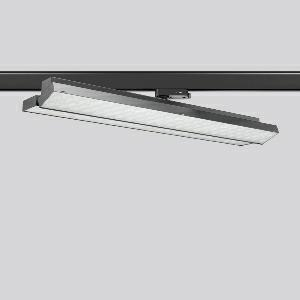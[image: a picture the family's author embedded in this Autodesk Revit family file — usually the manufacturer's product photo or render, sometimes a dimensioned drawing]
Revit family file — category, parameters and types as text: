
# Revit family: tx-move_742161_003_1_d967
name_source: partatom
category: Lighting Fixtures
units: mm (PartAtom-declared; Revit-internal decimal feet)

## family parameters
Cut with Voids When Loaded = No
Host = Face
Light Source = No
Part Type = Normal
Room Calculation Point = No
Round Connector Dimension = Use Diameter
Shared = No

## types (1)
- MultiLumen 1 (1 x LED Modul 840, 3125 lm, 4000)
    Apparent Load = 41 VA
    CIE Flux Codes = 90 97 99 100 100
    Color Rendering = 80
    Color Temperature = 4000
    Default Elevation = 1800 mm
    Description = Series: TX-MOVE
Multifunctional surface-mounted spotlight for area lighting. Very flat design. Housing: sheet steel, powder-coated. Rotation range: 356°. Swivel range: 90°. Consistent alignment possible with visible tilt scale. High-efficiency LED units with optimum light control thanks to clear plastic (PC) lens optics. Spezielle Mikrostrukturen reduzieren Gelbsaum. Symmetrical light distribution. With multi adaptor for 3-circuit tracks 230 V. Suitable for Track on ceiling. MultiLumen: Luminous flux adjustable in 3 steps. Factory setting is the highest luminous flux. Environmentally friendly and resource-saving due to replaceable and recyclable components. Very good glare control, ideal for till areas. 
Colour: deep black, matt (RAL 9005)
Length: 570 mm
Width: 119 mm
Height: 92 mm
Lamp: LED
Socket: without socket
Colour temperature: 4000K
Colour rendering index (CRI): 80
System power: 41 W
Rated luminous flux: 6250 lm
Luminous efficiency: 152 lm/W
System power 2: 57 W
Rated luminous flux 2: 8450 lm
Luminous efficiency 2: 148 lm/W
System power 3: 73 W
Rated luminous flux 3: 10400 lm
Luminous efficiency 3: 142 lm/W
Control gear: Regulated power supply
Protection class: I
Type of protection: IP 20
    Height = 75 mm
    Lamp = 1 x LED Modul 840
    Lamp Light Flux = 3125 lm
    Lamp count = 1
    Length = 569 mm
    Lifetime = 50000 h
    Luminous efficacy = 152 lm/W
    Manufacturer = RZB
    ModVariant = No
    Model = 742161.003.1
    Mounting Place = Ceiling
    Mounting Type = Surface mounted
    Number of Poles = 1
    OnlyDefault = Yes
    Power Factor = 1
    Product Name = TX-MOVE
    Product group = Track mounted projectors
    ProductGroupID = 301
    Protection Class = Protection class I
    Protection Degree = IP 20
    RLX_Detail_Level = 1
    RLX_Emergency_Light_Flux = 0 lm
    RLX_Emergency_Type = 0
    RLX_Emergency_Type_DB = No
    RlxData = <blob elided: 36973 chars, md5=0cfd9d59>
    Socket = socket
    Standby Power = 0 W
    System Light Flux = 6250 lm
    System Power = 41 W
    Type Comments = MultiLumen 1
    Type Image = 742162.003.jpg
    URL = http://relux.com
    VarID = multilumen_1
    Voltage = 0 V
    Weight = 0.00 kg
    Width = 119 mm

## geometry (parser evidence)
native form markers: Blend x4, Sweep x14
no freeform markers — native parametric forms only
